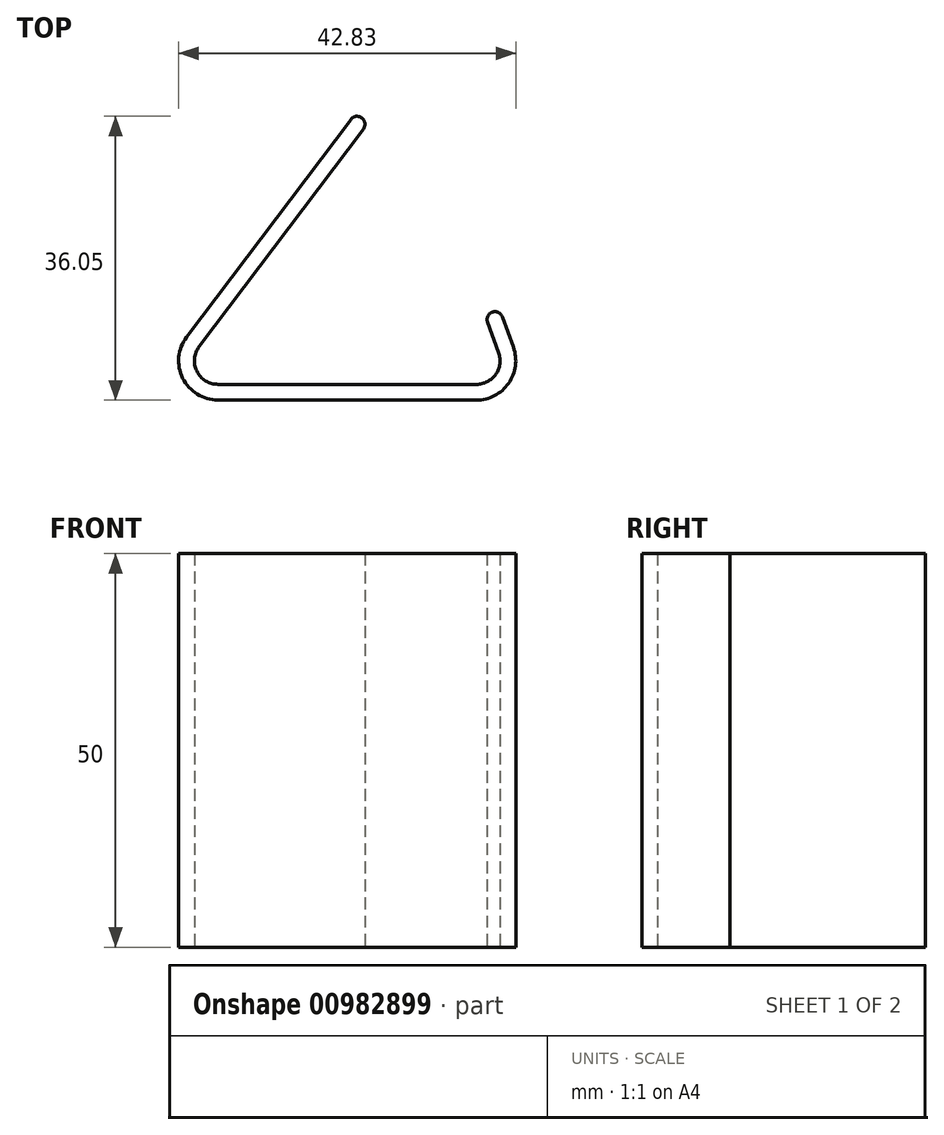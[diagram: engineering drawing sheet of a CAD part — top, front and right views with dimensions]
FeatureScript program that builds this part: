
annotation { "Feature Type Name" : "Feature", "Feature Type Description" : "" }
export const myFeature = defineFeature(function(context is Context, id is Id, definition is map)
    precondition{}
    {
        {
            var Q0;
            Q0=qCreatedBy(makeId("Top.planeOp"),FACE);
            var sketch = newSketch(context, id + "F0", { "sketchPlane" : qUnion([Q0])});
            skLineSegment(sketch, "E0", {"start": v(-21.9, -14.5) * mm, "end": v(-20.48, -18.37) * mm});
            skLineSegment(sketch, "E1", {"start": v(-25.18, -25.08) * mm, "end": v(-58, -25.08) * mm});
            skLineSegment(sketch, "E2", {"start": v(-62, -17.07) * mm, "end": v(-41.14, 10.58) * mm});
            skLineSegment(sketch, "E3.0", {"start": v(-60.4, -18.27) * mm, "end": v(-39.55, 9.37) * mm});
            skLineSegment(sketch, "E3.1", {"start": v(-25.18, -23.08) * mm, "end": v(-58, -23.08) * mm});
            skLineSegment(sketch, "E3.2", {"start": v(-23.77, -15.2) * mm, "end": v(-22.36, -19.05) * mm});
            skPoint(sketch, "E4.visualSharp", {"position": v(-64.03, -23.08) * mm});
            skArc(sketch, "E4.filletArc", {"start": v(-60.4, -18.27) * mm, "mid": v(-60.7, -21.42) * mm, "end": v(-58, -23.08) * mm});
            skPoint(sketch, "E5.visualSharp", {"position": v(-20.9, -23.08) * mm});
            skArc(sketch, "E5.filletArc", {"start": v(-25.18, -23.08) * mm, "mid": v(-22.73, -21.8) * mm, "end": v(-22.36, -19.05) * mm});
            skPoint(sketch, "E6.visualSharp", {"position": v(-68.04, -25.08) * mm});
            skArc(sketch, "E6.filletArc", {"start": v(-62, -17.07) * mm, "mid": v(-62.48, -22.3) * mm, "end": v(-58, -25.08) * mm});
            skPoint(sketch, "E7.visualSharp", {"position": v(-18.04, -25.08) * mm});
            skArc(sketch, "E7.filletArc", {"start": v(-25.18, -25.08) * mm, "mid": v(-21.09, -22.95) * mm, "end": v(-20.48, -18.37) * mm});
            skLineSegment(sketch, "E8", {"start": v(-39.74, 10.77) * mm, "end": v(-39.74, 10.77) * mm});
            skLineSegment(sketch, "E9", {"start": v(-23.17, -13.91) * mm, "end": v(-23.17, -13.91) * mm});
            skPoint(sketch, "E10.visualSharp", {"position": v(-40.54, 11.38) * mm});
            skArc(sketch, "E10.filletArc", {"start": v(-39.74, 10.77) * mm, "mid": v(-40.48, 10.96) * mm, "end": v(-41.14, 10.58) * mm});
            skPoint(sketch, "E11.visualSharp", {"position": v(-38.95, 10.17) * mm});
            skArc(sketch, "E11.filletArc", {"start": v(-39.55, 9.37) * mm, "mid": v(-39.36, 10.11) * mm, "end": v(-39.74, 10.77) * mm});
            skPoint(sketch, "E12.visualSharp", {"position": v(-24.11, -14.25) * mm});
            skArc(sketch, "E12.filletArc", {"start": v(-23.17, -13.91) * mm, "mid": v(-23.74, -14.43) * mm, "end": v(-23.77, -15.2) * mm});
            skPoint(sketch, "E13.visualSharp", {"position": v(-22.23, -13.57) * mm});
            skArc(sketch, "E13.filletArc", {"start": v(-21.9, -14.5) * mm, "mid": v(-22.4, -13.94) * mm, "end": v(-23.17, -13.91) * mm});
            skSolve(sketch);
        }
        {
            var Q0;
            Q0=makeQuery(id+"F0.imprint","IMPRINT",FACE,{"disambiguationData":[TD([[makeQuery(id+"F0.imprint","IMPRINT",EDGE,{"derivedFrom":sQuery(id+"F0.wireOp",EDGE,"E0")}),-1.0]])]});
            extrude(context, id + "F1", {"entities" : qUnion([Q0]), "depth" : 50 * mm, "offsetDistance" : 25 * mm});
        }
    });
